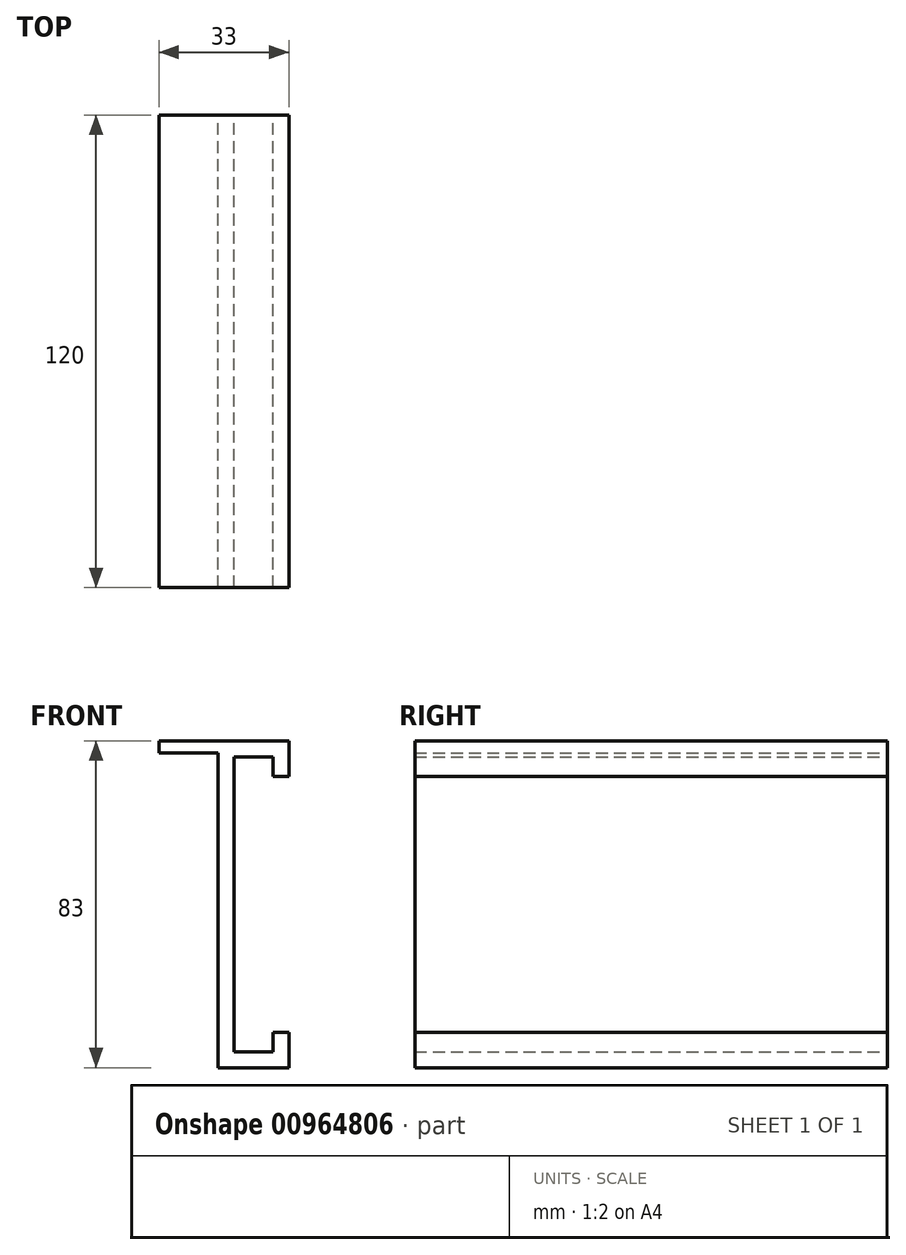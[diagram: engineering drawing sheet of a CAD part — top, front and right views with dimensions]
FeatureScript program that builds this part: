
annotation { "Feature Type Name" : "Feature", "Feature Type Description" : "" }
export const myFeature = defineFeature(function(context is Context, id is Id, definition is map)
    precondition{}
    {
        {
            var Q0;
            Q0=qCreatedBy(makeId("Front.planeOp"),FACE);
            var sketch = newSketch(context, id + "F0", { "sketchPlane" : qUnion([Q0])});
            skLineSegment(sketch, "E0", {"start": v(0, 63.57) * mm, "end": v(0, -48.43) * mm, "construction": true});
            skLineSegment(sketch, "E1", {"start": v(-57.29, 0) * mm, "end": v(59.86, 0) * mm, "construction": true});
            skLineSegment(sketch, "E2", {"start": v(12.18, -38.84) * mm, "end": v(12.18, -43.84) * mm});
            skLineSegment(sketch, "E3", {"start": v(12.18, -43.84) * mm, "end": v(2.18, -43.84) * mm});
            skLineSegment(sketch, "E4", {"start": v(2.18, -43.84) * mm, "end": v(2.18, 31.16) * mm});
            skLineSegment(sketch, "E5", {"start": v(2.18, 31.16) * mm, "end": v(12.18, 31.16) * mm});
            skLineSegment(sketch, "E6", {"start": v(12.18, 31.16) * mm, "end": v(12.18, 26.16) * mm});
            skLineSegment(sketch, "E7", {"start": v(12.18, 26.16) * mm, "end": v(16.18, 26.16) * mm});
            skLineSegment(sketch, "E8", {"start": v(16.18, 26.16) * mm, "end": v(16.18, 35.16) * mm});
            skLineSegment(sketch, "E9", {"start": v(16.18, 35.16) * mm, "end": v(-1.82, 35.16) * mm});
            skLineSegment(sketch, "E10", {"start": v(-1.82, 35.16) * mm, "end": v(-1.82, -47.84) * mm});
            skLineSegment(sketch, "E11", {"start": v(-1.82, -47.84) * mm, "end": v(16.18, -47.84) * mm});
            skLineSegment(sketch, "E12", {"start": v(16.18, -47.84) * mm, "end": v(16.18, -38.84) * mm});
            skLineSegment(sketch, "E13", {"start": v(16.18, -38.84) * mm, "end": v(12.18, -38.84) * mm});
            skLineSegment(sketch, "E14", {"start": v(-1.82, 35.16) * mm, "end": v(-16.82, 35.16) * mm});
            skLineSegment(sketch, "E15", {"start": v(-16.82, 35.16) * mm, "end": v(-16.82, 32.16) * mm});
            skLineSegment(sketch, "E16", {"start": v(-16.82, 32.16) * mm, "end": v(-1.82, 32.16) * mm});
            skSolve(sketch);
        }
        {
            var Q0;
            Q0 = qSketchRegion(id + "F0", true);
            extrude(context, id + "F1", {"entities" : qUnion([Q0]), "depth" : 120 * mm, "offsetDistance" : 25 * mm});
        }
    });
